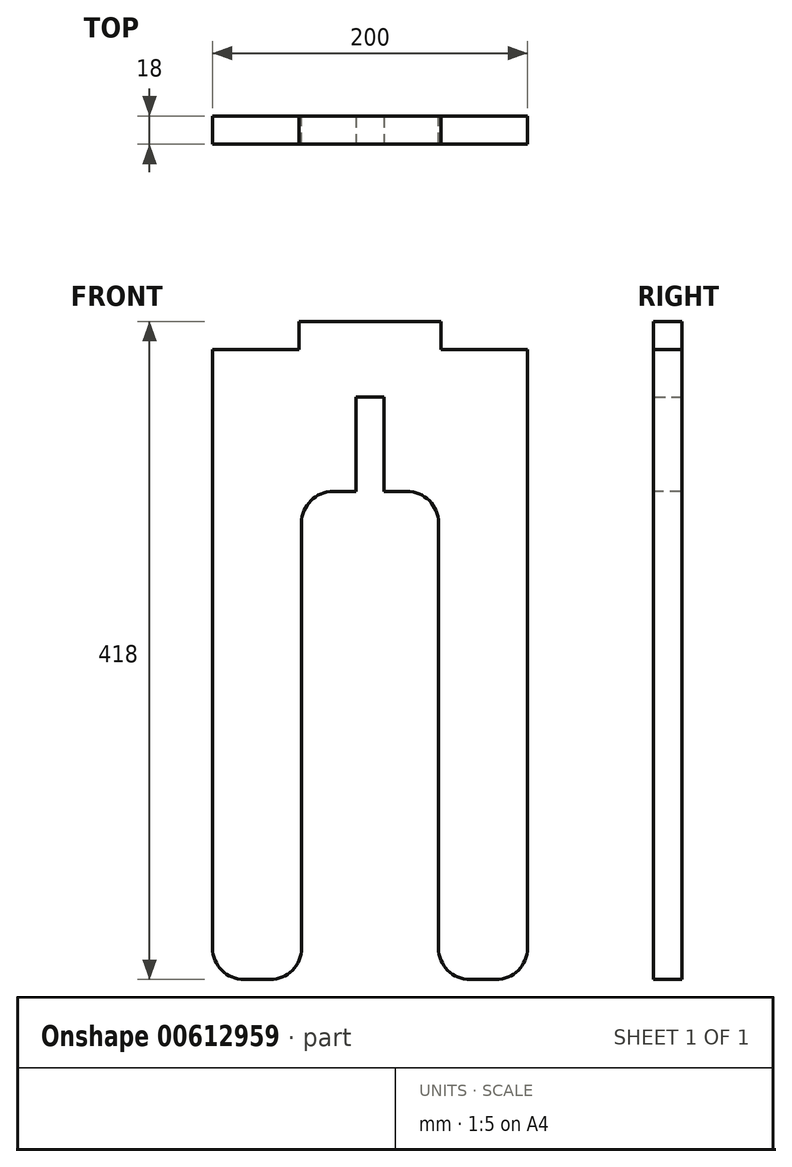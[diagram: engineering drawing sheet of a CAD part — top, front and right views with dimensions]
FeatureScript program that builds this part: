
annotation { "Feature Type Name" : "Feature", "Feature Type Description" : "" }
export const myFeature = defineFeature(function(context is Context, id is Id, definition is map)
    precondition{}
    {
        {
            var Q0;
            Q0=qCreatedBy(makeId("Front.planeOp"),FACE);
            var sketch = newSketch(context, id + "F0", { "sketchPlane" : qUnion([Q0])});
            skLineSegment(sketch, "E0.bottom", {"start": v(80, -200) * mm, "end": v(63.48, -200) * mm});
            skLineSegment(sketch, "E0.top", {"start": v(100, 200) * mm, "end": v(45, 200) * mm});
            skLineSegment(sketch, "E0.left", {"start": v(100, -180) * mm, "end": v(100, 200) * mm});
            skLineSegment(sketch, "E0.right", {"start": v(-100, -180) * mm, "end": v(-100, 200) * mm});
            skPoint(sketch, "E0.middle", {"position": v(0, 0) * mm});
            skLineSegment(sketch, "E1.top", {"start": v(23.48, 110) * mm, "end": v(-23.48, 110) * mm});
            skLineSegment(sketch, "E1.left", {"start": v(43.48, -110) * mm, "end": v(43.48, 90) * mm});
            skLineSegment(sketch, "E1.right", {"start": v(-43.48, -110) * mm, "end": v(-43.48, 90) * mm});
            skLineSegment(sketch, "E2", {"start": v(-43.48, -110) * mm, "end": v(-43.48, -180) * mm});
            skLineSegment(sketch, "E3", {"start": v(43.48, -180) * mm, "end": v(43.48, -110) * mm});
            skLineSegment(sketch, "E4.trimOffspring", {"start": v(-63.48, -200) * mm, "end": v(-80, -200) * mm});
            skPoint(sketch, "E5.orphan", {"position": v(43.48, -292.06) * mm});
            skPoint(sketch, "E6.visualSharp", {"position": v(-43.48, -200) * mm});
            skArc(sketch, "E6.filletArc", {"start": v(-63.48, -200) * mm, "mid": v(-49.34, -194.14) * mm, "end": v(-43.48, -180) * mm});
            skPoint(sketch, "E7.visualSharp", {"position": v(43.48, -200) * mm});
            skArc(sketch, "E7.filletArc", {"start": v(43.48, -180) * mm, "mid": v(49.34, -194.14) * mm, "end": v(63.48, -200) * mm});
            skPoint(sketch, "E8.visualSharp", {"position": v(100, -200) * mm});
            skArc(sketch, "E8.filletArc", {"start": v(80, -200) * mm, "mid": v(94.14, -194.14) * mm, "end": v(100, -180) * mm});
            skPoint(sketch, "E9.visualSharp", {"position": v(-100, -200) * mm});
            skArc(sketch, "E9.filletArc", {"start": v(-100, -180) * mm, "mid": v(-94.14, -194.14) * mm, "end": v(-80, -200) * mm});
            skPoint(sketch, "E10.visualSharp", {"position": v(43.48, 110) * mm});
            skArc(sketch, "E10.filletArc", {"start": v(43.48, 90) * mm, "mid": v(37.62, 104.14) * mm, "end": v(23.48, 110) * mm});
            skPoint(sketch, "E11.visualSharp", {"position": v(-43.48, 110) * mm});
            skArc(sketch, "E11.filletArc", {"start": v(-23.48, 110) * mm, "mid": v(-37.62, 104.14) * mm, "end": v(-43.48, 90) * mm});
            skLineSegment(sketch, "E12.trimOffspring", {"start": v(45, 200) * mm, "end": v(45, 218) * mm});
            skLineSegment(sketch, "E13.trimOffspring", {"start": v(-45, 200) * mm, "end": v(-45, 218) * mm});
            skLineSegment(sketch, "E14.trimOffspring", {"start": v(-45, 200) * mm, "end": v(-100, 200) * mm});
            skLineSegment(sketch, "E15", {"start": v(-45, 218) * mm, "end": v(45, 218) * mm});
            skSolve(sketch);
        }
        {
            var Q0;
            Q0=makeQuery(id+"F0.imprint","IMPRINT",FACE,{"disambiguationData":[TD([[makeQuery(id+"F0.imprint","IMPRINT",EDGE,{"derivedFrom":sQuery(id+"F0.wireOp",EDGE,"E0.bottom")}),-1.0]])]});
            var sketch = newSketch(context, id + "F1", { "sketchPlane" : qUnion([Q0])});
            skLineSegment(sketch, "E16.bottom", {"start": v(-9, 170.05) * mm, "end": v(9, 170.05) * mm});
            skLineSegment(sketch, "E16.left", {"start": v(-9, 170.05) * mm, "end": v(-9, 110.05) * mm});
            skLineSegment(sketch, "E16.right", {"start": v(9, 170.05) * mm, "end": v(9, 110.05) * mm});
            skPoint(sketch, "E16.middle", {"position": v(0, 110.05) * mm});
            skLineSegment(sketch, "E17", {"start": v(0, 110.05) * mm, "end": v(9, 110.05) * mm});
            skLineSegment(sketch, "E18", {"start": v(9, 110.05) * mm, "end": v(-9, 110.05) * mm});
            skPoint(sketch, "E19.orphan", {"position": v(-9, 50.05) * mm});
            skPoint(sketch, "E20.orphan", {"position": v(9, 50.05) * mm});
            skLineSegment(sketch, "E21.left", {"start": v(-9, 170.05) * mm, "end": v(-9, 170.05) * mm});
            skLineSegment(sketch, "E21.right", {"start": v(9, 170.05) * mm, "end": v(9, 170.05) * mm});
            skLineSegment(sketch, "E22.top", {"start": v(-9, 70.05) * mm, "end": v(9, 70.05) * mm});
            skLineSegment(sketch, "E22.left", {"start": v(-9, 170.05) * mm, "end": v(-9, 70.05) * mm});
            skLineSegment(sketch, "E22.right", {"start": v(9, 170.05) * mm, "end": v(9, 70.05) * mm});
            skSolve(sketch);
        }
        {
            var Q0;
            Q0 = qSketchRegion(id + "F0", true);
            extrude(context, id + "F2", {"entities" : qUnion([Q0]), "depth" : 18 * mm, "offsetDistance" : 25 * mm});
        }
        {
            var Q0;
            Q0 = qSketchRegion(id + "F1", true);
            extrude(context, id + "F3", {"entities" : qUnion([Q0]), "operationType" : NewBodyOperationType.REMOVE, "depth" : 188 * mm, "offsetDistance" : 25 * mm});
        }
    });
